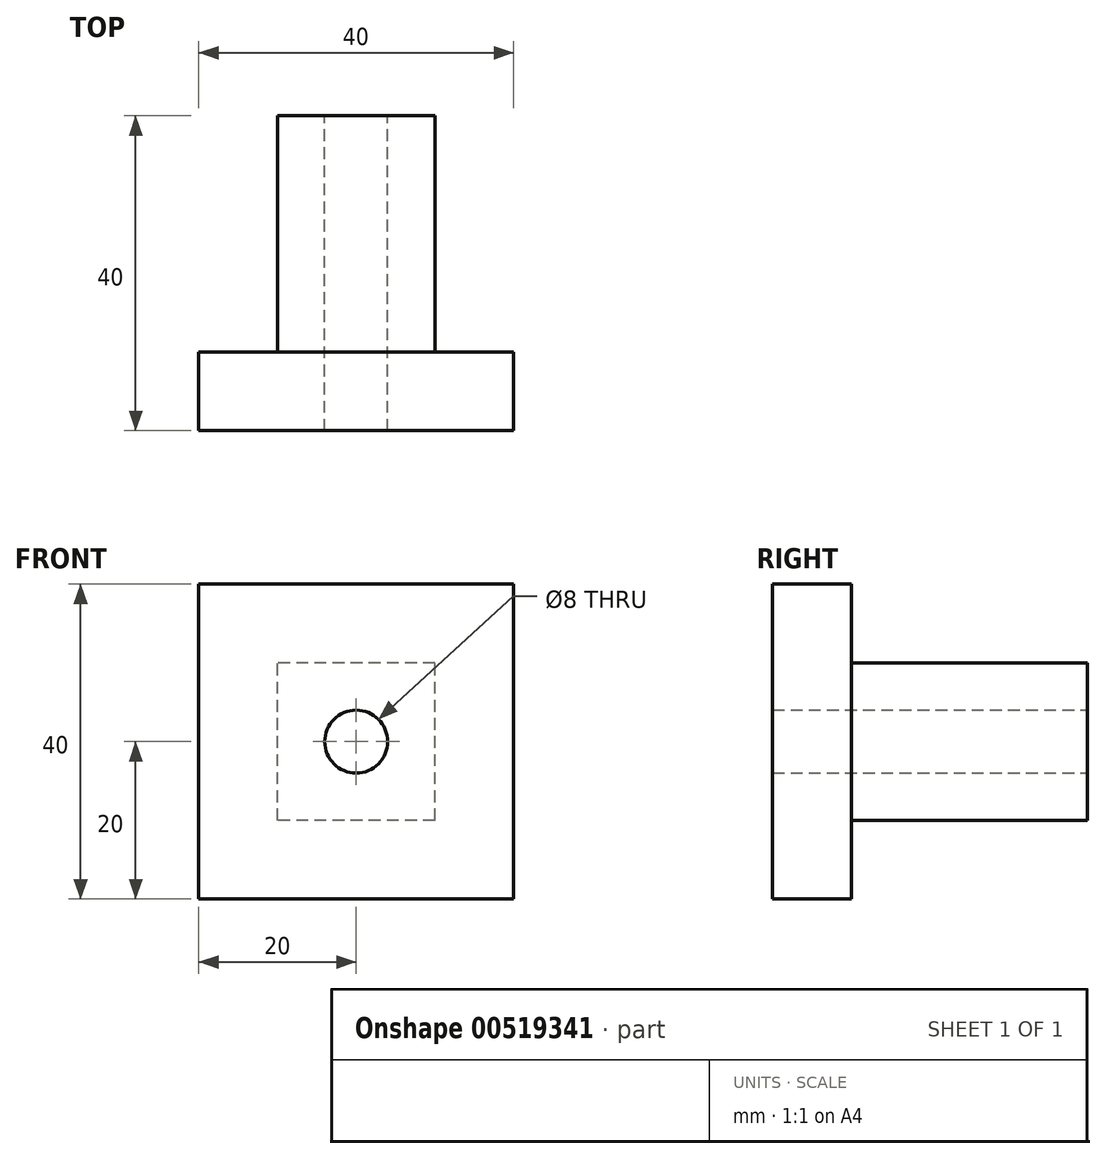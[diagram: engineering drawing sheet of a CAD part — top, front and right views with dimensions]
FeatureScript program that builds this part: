
annotation { "Feature Type Name" : "Feature", "Feature Type Description" : "" }
export const myFeature = defineFeature(function(context is Context, id is Id, definition is map)
    precondition{}
    {
        {
            var Q0;
            Q0=qCreatedBy(makeId("Front.planeOp"),FACE);
            var sketch = newSketch(context, id + "F0", { "sketchPlane" : qUnion([Q0])});
            skLineSegment(sketch, "E0.bottom", {"start": v(20, -20) * mm, "end": v(-20, -20) * mm});
            skLineSegment(sketch, "E0.top", {"start": v(20, 20) * mm, "end": v(-20, 20) * mm});
            skLineSegment(sketch, "E0.left", {"start": v(20, -20) * mm, "end": v(20, 20) * mm});
            skLineSegment(sketch, "E0.right", {"start": v(-20, -20) * mm, "end": v(-20, 20) * mm});
            skPoint(sketch, "E0.middle", {"position": v(0, 0) * mm});
            skCircle(sketch, "E1", {"center": v(0, 0) * mm, "radius": 4 * mm});
            skSolve(sketch);
        }
        {
            var Q0;
            Q0 = qSketchRegion(id + "F0", true);
            extrude(context, id + "F1", {"entities" : qUnion([Q0]), "depth" : 10 * mm, "offsetDistance" : 25 * mm});
        }
        {
            var Q0;
            Q0=qCreatedBy(makeId("Front.planeOp"),FACE);
            var sketch = newSketch(context, id + "F2", { "sketchPlane" : qUnion([Q0])});
            skLineSegment(sketch, "E2.bottom", {"start": v(10, -10) * mm, "end": v(-10, -10) * mm});
            skLineSegment(sketch, "E2.top", {"start": v(10, 10) * mm, "end": v(-10, 10) * mm});
            skLineSegment(sketch, "E2.left", {"start": v(10, -10) * mm, "end": v(10, 10) * mm});
            skLineSegment(sketch, "E2.right", {"start": v(-10, -10) * mm, "end": v(-10, 10) * mm});
            skPoint(sketch, "E2.middle", {"position": v(0, 0) * mm});
            skCircle(sketch, "E3", {"center": v(0, 0) * mm, "radius": 4 * mm});
            skSolve(sketch);
        }
        {
            var Q0;
            Q0 = qSketchRegion(id + "F2", true);
            extrude(context, id + "F3", {"entities" : qUnion([Q0]), "operationType" : NewBodyOperationType.ADD, "oppositeDirection" : true, "depth" : 30 * mm, "offsetDistance" : 25 * mm});
        }
    });
